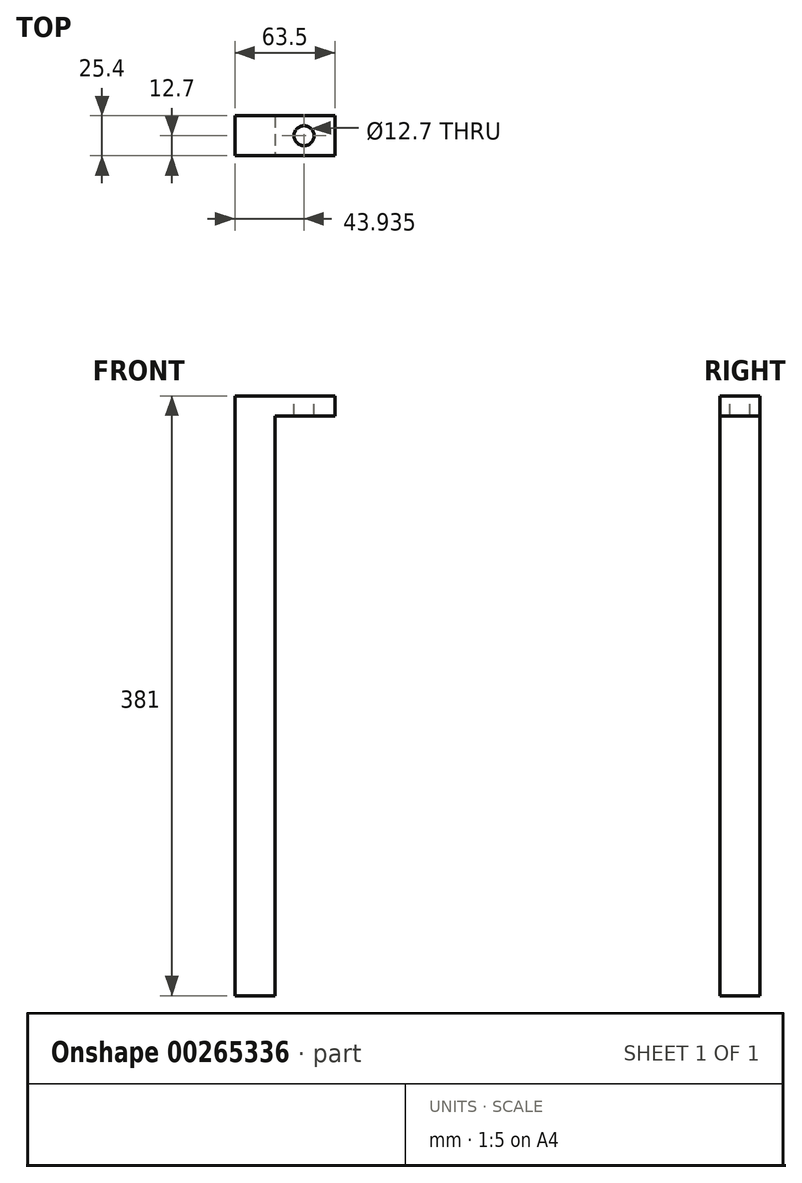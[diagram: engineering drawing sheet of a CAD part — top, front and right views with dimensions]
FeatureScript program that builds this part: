
annotation { "Feature Type Name" : "Feature", "Feature Type Description" : "" }
export const myFeature = defineFeature(function(context is Context, id is Id, definition is map)
    precondition{}
    {
        {
            var Q0;
            Q0=qCreatedBy(makeId("Front.planeOp"),FACE);
            var sketch = newSketch(context, id + "F0", { "sketchPlane" : qUnion([Q0])});
            skLineSegment(sketch, "E0.bottom", {"start": v(-110.45, 190.7) * mm, "end": v(-85.05, 190.7) * mm});
            skLineSegment(sketch, "E0.top", {"start": v(-110.45, -190.3) * mm, "end": v(-85.05, -190.3) * mm});
            skLineSegment(sketch, "E0.left", {"start": v(-110.45, 190.7) * mm, "end": v(-110.45, -190.3) * mm});
            skLineSegment(sketch, "E0.right", {"start": v(-85.05, 190.7) * mm, "end": v(-85.05, -190.3) * mm});
            skLineSegment(sketch, "E1.bottom", {"start": v(-85.05, 190.7) * mm, "end": v(-46.95, 190.7) * mm});
            skLineSegment(sketch, "E1.top", {"start": v(-85.05, 178) * mm, "end": v(-46.95, 178) * mm});
            skLineSegment(sketch, "E1.left", {"start": v(-85.05, 190.7) * mm, "end": v(-85.05, 178) * mm});
            skLineSegment(sketch, "E1.right", {"start": v(-46.95, 190.7) * mm, "end": v(-46.95, 178) * mm});
            skSolve(sketch);
        }
        {
            var Q0;
            Q0=makeQuery(id+"F0.imprint","IMPRINT",FACE,{"disambiguationData":[TD([[makeQuery(id+"F0.imprint","IMPRINT",EDGE,{"derivedFrom":sQuery(id+"F0.wireOp",EDGE,"E1.bottom")}),-1.0]])]});
            var Q1;
            Q1=makeQuery(id+"F0.imprint","IMPRINT",FACE,{"disambiguationData":[TD([[makeQuery(id+"F0.imprint","IMPRINT",EDGE,{"derivedFrom":sQuery(id+"F0.wireOp",EDGE,"E0.bottom")}),-1.0]])]});
            extrude(context, id + "F1", {"entities" : qUnion([Q0, Q1]), "endBound" : BoundingType.SYMMETRIC, "oppositeDirection" : true, "depth" : 25.4 * mm});
        }
        {
            var Q0;
            Q0=makeQuery(id+"F1.opExtrude","SWEPT_FACE",FACE,{"disambiguationData":[OSD([sQuery(id+"F0.wireOp",EDGE,"E0.bottom"),sQuery(id+"F0.wireOp",EDGE,"E1.bottom")])]});
            var sketch = newSketch(context, id + "F2", { "sketchPlane" : qUnion([Q0])});
            skPoint(sketch, "E2", {"position": v(-66.51, 0) * mm});
            skSolve(sketch);
        }
        {
            var Q0;
            Q0=sQuery(id+"F2.wireOp",VERTEX,"E2");
            var Q1;
            Q1=makeQuery(id+"F1.opExtrude","SWEPT_BODY",BODY,{"disambiguationData":[OSD([sQuery(id+"F0.wireOp",EDGE,"E0.bottom"),sQuery(id+"F0.wireOp",EDGE,"E0.top"),sQuery(id+"F0.wireOp",EDGE,"E0.left"),sQuery(id+"F0.wireOp",EDGE,"E0.right"),sQuery(id+"F0.wireOp",EDGE,"E1.bottom"),sQuery(id+"F0.wireOp",EDGE,"E1.top"),sQuery(id+"F0.wireOp",EDGE,"E1.right")])]});
            hole(context, id + "F3", {"style" : HoleStyle.SIMPLE, "endStyle" : HoleEndStyle.THROUGH, "holeDiameter" : 12.7 * mm, "tappedDepth" : 12.7 * mm, "tapClearance" : 3, "locations" : qUnion([Q0]), "scope" : qUnion([Q1])});
        }
    });
